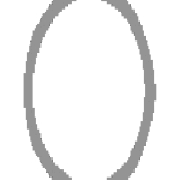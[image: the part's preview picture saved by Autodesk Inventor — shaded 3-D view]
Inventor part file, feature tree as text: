
AUTODESK INVENTOR PART (.ipt)
format: ipt  version: 2021 (Build 250183000, 183)  size: 117,760 bytes
history: native  units: in
note: dims shown in document units (in); Inventor stores cm internally (conversion verified against a paired STEP export)
features: other x4, sketch x3, plane x1
ambient origin geometry x8: Origin, YZ Plane, XZ Plane, XY Plane, X Axis, Y Axis, Z Axis, Center Point
bodies: Solid1 (feature_tree), Body (feature_tree)
feature tree (8):
  other  "Driven Length"
  other  "Frame Generator"
  other  "Start Plane"
  other  "End Plane"
  sketch  "Sketch"  dims[d2=1.3416in d4=-0.0in d5=1.3416in d6=0.12in d7=0.0in d8=90.0deg d9=1.3416in]
  sketch  "Sketch2"  dims[d0=1.0in]
  plane  "Work Plane3"
  sketch  "Sketch3"  dims[d1=0.065in]
